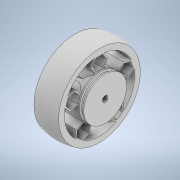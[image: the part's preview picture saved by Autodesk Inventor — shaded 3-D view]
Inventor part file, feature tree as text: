
AUTODESK INVENTOR PART (.ipt)
format: ipt  version: 2020 (Build 240168000, 168)  size: 512,512 bytes
history: native  units: in
note: dims shown in document units (in); Inventor stores cm internally (conversion verified against a paired STEP export)
features: sketch x7, extrude x3, revolve x2, loft x1, projected_geometry x1
ambient origin geometry x8: Origin, YZ Plane, XZ Plane, XY Plane, X Axis, Y Axis, Z Axis, Center Point
bodies: Solid1 (feature_tree)
feature tree (14):
  extrude  "Extrusion1"  Depth=0.0394in
  sketch  "Sketch3"  dims[d6=0.8858in d7=0.1181in]
  revolve  "Revolution1"  [1 undecoded]
  extrude  "Extrusion2"  Depth=0.1181in
  revolve  "Revolution2"  [1 undecoded]
  sketch  "Sketch5"  dims[d10=0.1181in d16=0.5118in]
  sketch  "Sketch6"  dims[d17=0.0in d19=90.0deg]
  sketch  "Sketch7"  dims[d20=0.0394in d22=60.0deg d24=0.0394in d25=90.0deg d26=60.0deg d27=0.1181in d32=0.0157in d33=0.0157in d34=0.0157in d35=0.0157in d40=1.9685in d42=360.0deg d48=0.0in d49=90.0deg d50=0.0in d51=90.0deg d52=0.0in d53=0.0in]
  loft  "Loft2"
  extrude  "Extrusion3"  TaperAngle=90.0deg  [1 undecoded]
  sketch  "Sketch1"  dims[d0=0.1181in d1=0.0394in]
  sketch  "Sketch2"  dims[d3=1.6929in d4=0.1181in]
  projected_geometry  "Projected Loop1"
  sketch  "Sketch4"  dims[d8=0.0in d9=1.6929in]
note: 3 required parameter values undecoded (feature->parameter linkage not recoverable at this tier; creation-order binding heuristic only, values carry confidence <= 0.55)